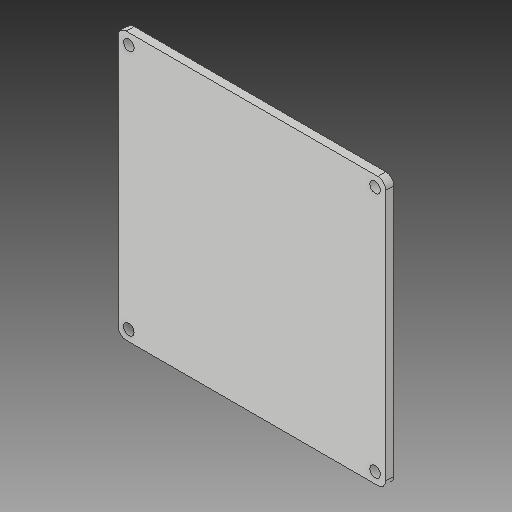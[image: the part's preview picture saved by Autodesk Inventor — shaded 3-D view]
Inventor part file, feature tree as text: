
AUTODESK INVENTOR PART (.ipt)
format: ipt  version: 2017 (Build 210142000, 142)  size: 116,736 bytes
history: native  units: mm
features: extrude x1, sketch x1
ambient origin geometry x8: Origin, YZ Plane, XZ Plane, XY Plane, X Axis, Y Axis, Z Axis, Center Point
bodies: Body1 (feature_tree)
feature tree (2):
  extrude  "Extrusion2"  Depth=100.0mm
  sketch  "Sketch1"  dims[d0=100.0mm d1=100.0mm d4=4.0mm d5=3.0mm d6=4.0mm d7=3.0mm d8=0.0mm]
